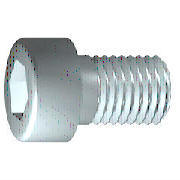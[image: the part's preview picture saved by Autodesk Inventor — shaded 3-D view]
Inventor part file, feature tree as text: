
AUTODESK INVENTOR PART (.ipt)
format: ipt  version: 2021.2 (Build 252289000, 289)  size: 186,880 bytes
history: native  units: mm (DEFAULTED — no unit token found)
features: sketch x2, other x1, extrude x1, plane x1, fillet x1
ambient origin geometry x7: Origin, YZ Plane, XY Plane, X Axis, Y Axis, Z Axis, Center Point
bodies: Solid1 (feature_tree)
feature tree (6):
  other  "Базовый элемент"
  extrude  "Паз"  Depth=20.0mm
  plane  "Work Plane1"
  fillet  "Fillet2"  Radius=0.429515mm
  sketch  "Эскиз1"
  sketch  "Эскиз2"
